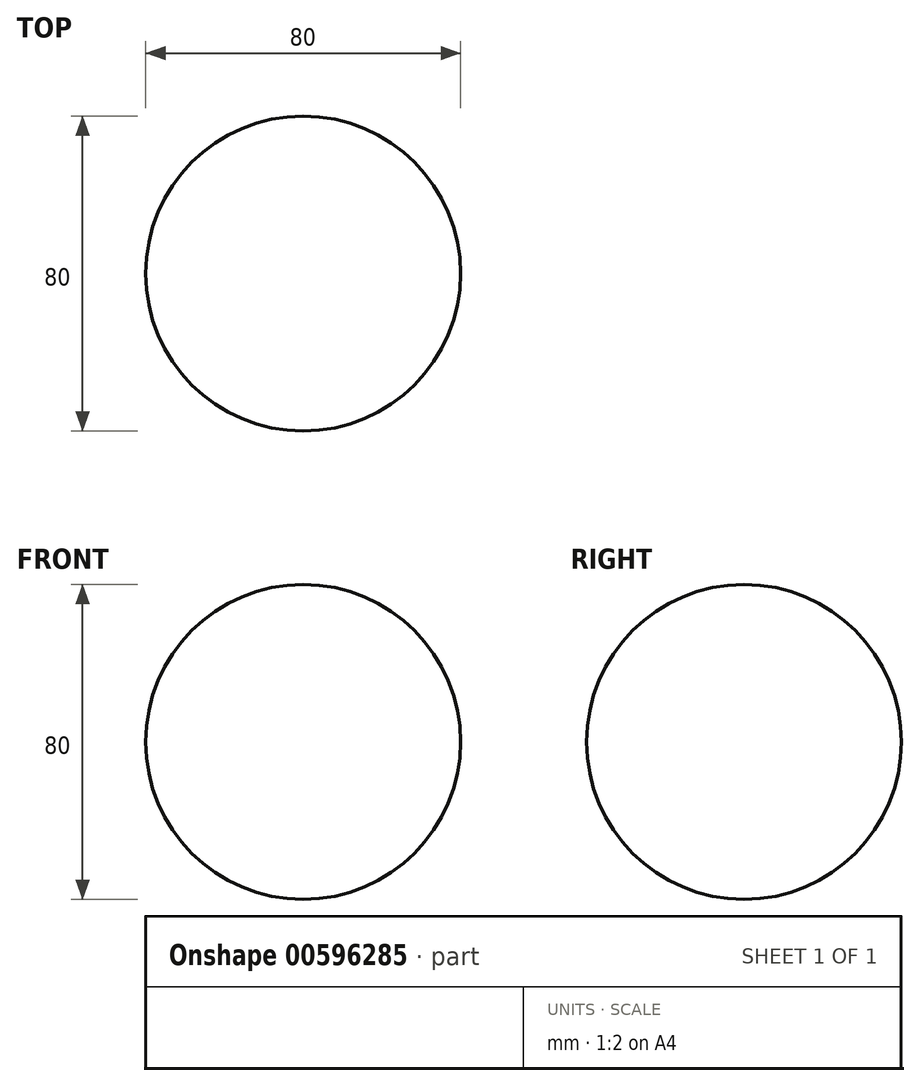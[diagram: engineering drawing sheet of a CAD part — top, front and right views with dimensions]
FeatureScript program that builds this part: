
annotation { "Feature Type Name" : "Feature", "Feature Type Description" : "" }
export const myFeature = defineFeature(function(context is Context, id is Id, definition is map)
    precondition{}
    {
        {
            var Q0;
            Q0=qCreatedBy(makeId("Front.planeOp"),FACE);
            var sketch = newSketch(context, id + "F0", { "sketchPlane" : qUnion([Q0])});
            skArc(sketch, "E0", {"start": v(0, -40) * mm, "mid": v(40, 0) * mm, "end": v(0, 40) * mm});
            skLineSegment(sketch, "E1", {"start": v(0, -40) * mm, "end": v(0, 40) * mm});
            skSolve(sketch);
        }
        {
            var Q0;
            Q0=qCreatedBy(makeId("Front.planeOp"),FACE);
            var sketch = newSketch(context, id + "F1", { "sketchPlane" : qUnion([Q0])});
            skLineSegment(sketch, "E2", {"start": v(0, 52.56) * mm, "end": v(0, 0) * mm});
            skSolve(sketch);
        }
        {
            var Q0;
            Q0 = qSketchRegion(id + "F0", true);
            var Q1;
            Q1=sQuery(id+"F1.wireOp",EDGE,"E2");
            revolve(context, id + "F2", {"entities" : qUnion([Q0]), "axis" : qUnion([Q1]), "revolveType" : RevolveType.FULL});
        }
    });
